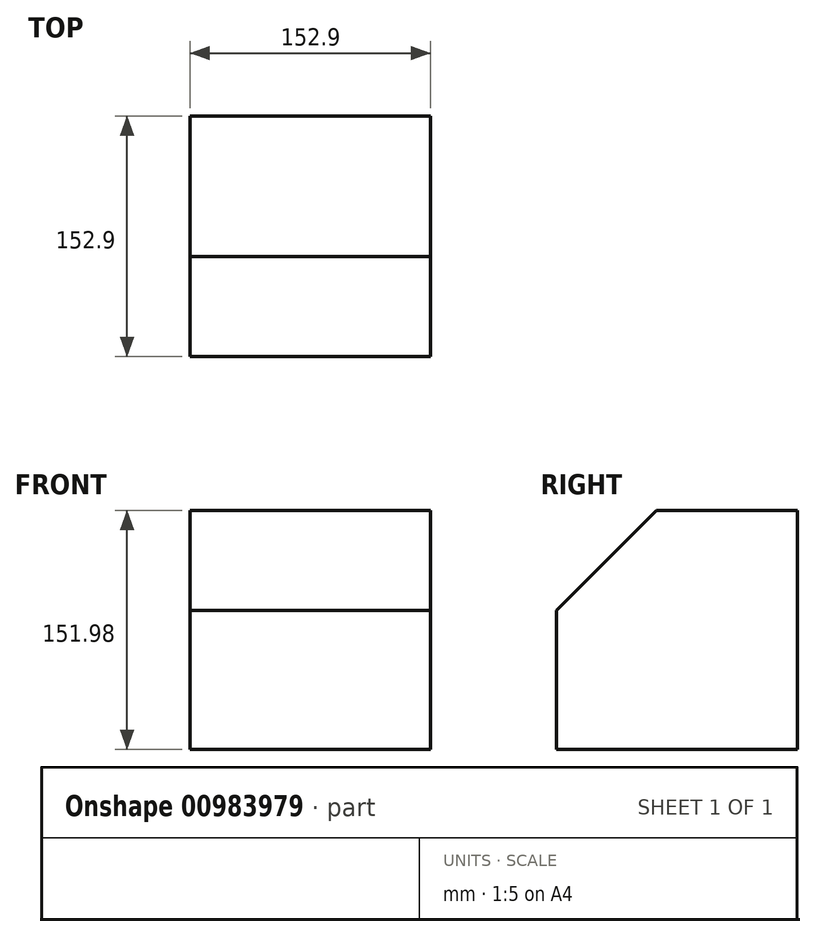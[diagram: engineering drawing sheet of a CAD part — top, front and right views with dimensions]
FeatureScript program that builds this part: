
annotation { "Feature Type Name" : "Feature", "Feature Type Description" : "" }
export const myFeature = defineFeature(function(context is Context, id is Id, definition is map)
    precondition{}
    {
        {
            var Q0;
            Q0=qCreatedBy(makeId("Front.planeOp"),FACE);
            var sketch = newSketch(context, id + "F0", { "sketchPlane" : qUnion([Q0])});
            skLineSegment(sketch, "E0.bottom", {"start": v(76.45, 75.99) * mm, "end": v(-76.45, 75.99) * mm});
            skLineSegment(sketch, "E0.top", {"start": v(76.45, -75.99) * mm, "end": v(-76.45, -75.99) * mm});
            skLineSegment(sketch, "E0.left", {"start": v(76.45, 75.99) * mm, "end": v(76.45, -75.99) * mm});
            skLineSegment(sketch, "E0.right", {"start": v(-76.45, 75.99) * mm, "end": v(-76.45, -75.99) * mm});
            skPoint(sketch, "E0.middle", {"position": v(0, 0) * mm});
            skSolve(sketch);
        }
        {
            var Q0;
            Q0 = qSketchRegion(id + "F0", true);
            extrude(context, id + "F1", {"entities" : qUnion([Q0]), "endBound" : BoundingType.SYMMETRIC, "depth" : 152.9 * mm, "offsetDistance" : 25.4 * mm});
        }
        {
            var Q0;
            Q0=makeQuery(id+"F1.opExtrude","CAP_EDGE",EDGE,{"disambiguationData":[OSD([sQuery(id+"F0.wireOp",EDGE,"E0.bottom")])],"isStart":false});
            chamfer(context, id + "F2", {"entities" : qUnion([Q0]), "width" : 63.5 * mm, "tangentPropagation" : true});
        }
    });
